# Revit family: Domotics-DomesticRanges-GEWISS-SYSTEM_POWER-SOCKET-OUTLET_SHAVER
name_source: partatom
category: Apparecchi elettrici
revit_build: Autodesk Revit 2016 (Build: 20161004_0715(x64)
units: mm (PartAtom-declared; Revit-internal decimal feet)

## family parameters
Condiviso = Sì
Host = Superficie
Mantenere orientamento annotazione = Sì
Punto di calcolo locali = Sì
Quota connettore circolare = Usa diametro
Taglio con vuoti quando caricato = No
Tipo di parte = Normale

## types (2) — shared parameters
Carico apparente = 0 VA
Catalogue = DOMOTICS
Catalogue Range = SYSTEM - DOMESTIC RANGE
Description. = Shaver socket-outlet
For plug pins = Ã˜ 4 / 5 - 6.3x1.5 mm
IDF = 5a220150-a835-44e3-b795-94ad5cb6ae16
IDT = 7bd01612-76f8-4d4d-9a05-785bbd72804f
Immagine tipo = GW21841.jpg
Maximum power = 20VA
N. poli = 1
No. SYSTEM modules = 3
Produttore = GEWISS S.p.A.
Prospetto di default = 1219 mm
SEO = Socket outlet
Selectable output voltage = 120 - 230V ac
Standard = Euro-USA
Standard: = Euro-USA
Supply voltage = 230V ac - 50/60 Hz
TIPO_ = System Presa Rasoio_GENERICO : GW21841 Presa per rasoio standard Euroamericano nero
Technical sheet = https://www.gewiss.com
Type = P11-USA
Type: = For razor
URL = https://www.gewiss.com
Version file RFA = 19.4
Volt = 230 V

## per-type parameters (varying)
| type | Colour | Descrizione | EAN code | Electrocod | Modello | Voltage | Voltage: |
| GW21841 - 230/120v euro/usa shaver socket black | Black | 230/120V EURO/USA SHAVER SOCKET SY/BK | 8011564129665 | 0131 | GW21841 | 230V ac | 230V ac |
| GW20841 - 230/120v euro/usa shaver socket white | White | 230/120V EURO/USA SHAVER SOCKET SY/WT | 8011564038585 | 0130 | GW20841 |  |  |

## geometry (parser evidence)
native form markers: Sweep x2
no freeform markers — native parametric forms only
